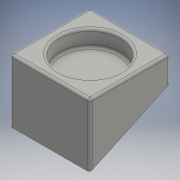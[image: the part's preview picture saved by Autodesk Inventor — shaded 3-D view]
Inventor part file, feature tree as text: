
AUTODESK INVENTOR PART (.ipt)
format: ipt  version: 2016 (Build 200138000, 138)  size: 167,424 bytes
history: native  units: in
note: dims shown in document units (in); Inventor stores cm internally (conversion verified against a paired STEP export)
features: fillet x3, sketch x3, extrude x2, hole x1
ambient origin geometry x8: Origin, YZ Plane, XZ Plane, XY Plane, X Axis, Y Axis, Z Axis, Center Point
bodies: Solid1 (feature_tree)
feature tree (9):
  extrude  "Extrusion1"  Depth=3.25in
  extrude  "Extrusion2"  TaperAngle=0.0deg  [1 undecoded]
  hole  "Hole2"  [1 undecoded]
  fillet  "Fillet1"  Radius=0.125in
  fillet  "Fillet2"  Radius=0.125in
  fillet  "Fillet3"  [1 undecoded]
  sketch  "Sketch1"  dims[d4=0.0in d5=3.25in]
  sketch  "Sketch2"  dims[d6=0.875in d7=0.0in]
  sketch  "Sketch4"  dims[d14=3.25in d22=0.307in d23=0.75in d24=0.375in d25=0.25in d26=0.5635in d27=0.875in d28=0.8108in d29=0.125in d30=0.125in d31=0.125in]
note: 3 required parameter values undecoded (feature->parameter linkage not recoverable at this tier; creation-order binding heuristic only, values carry confidence <= 0.55)
